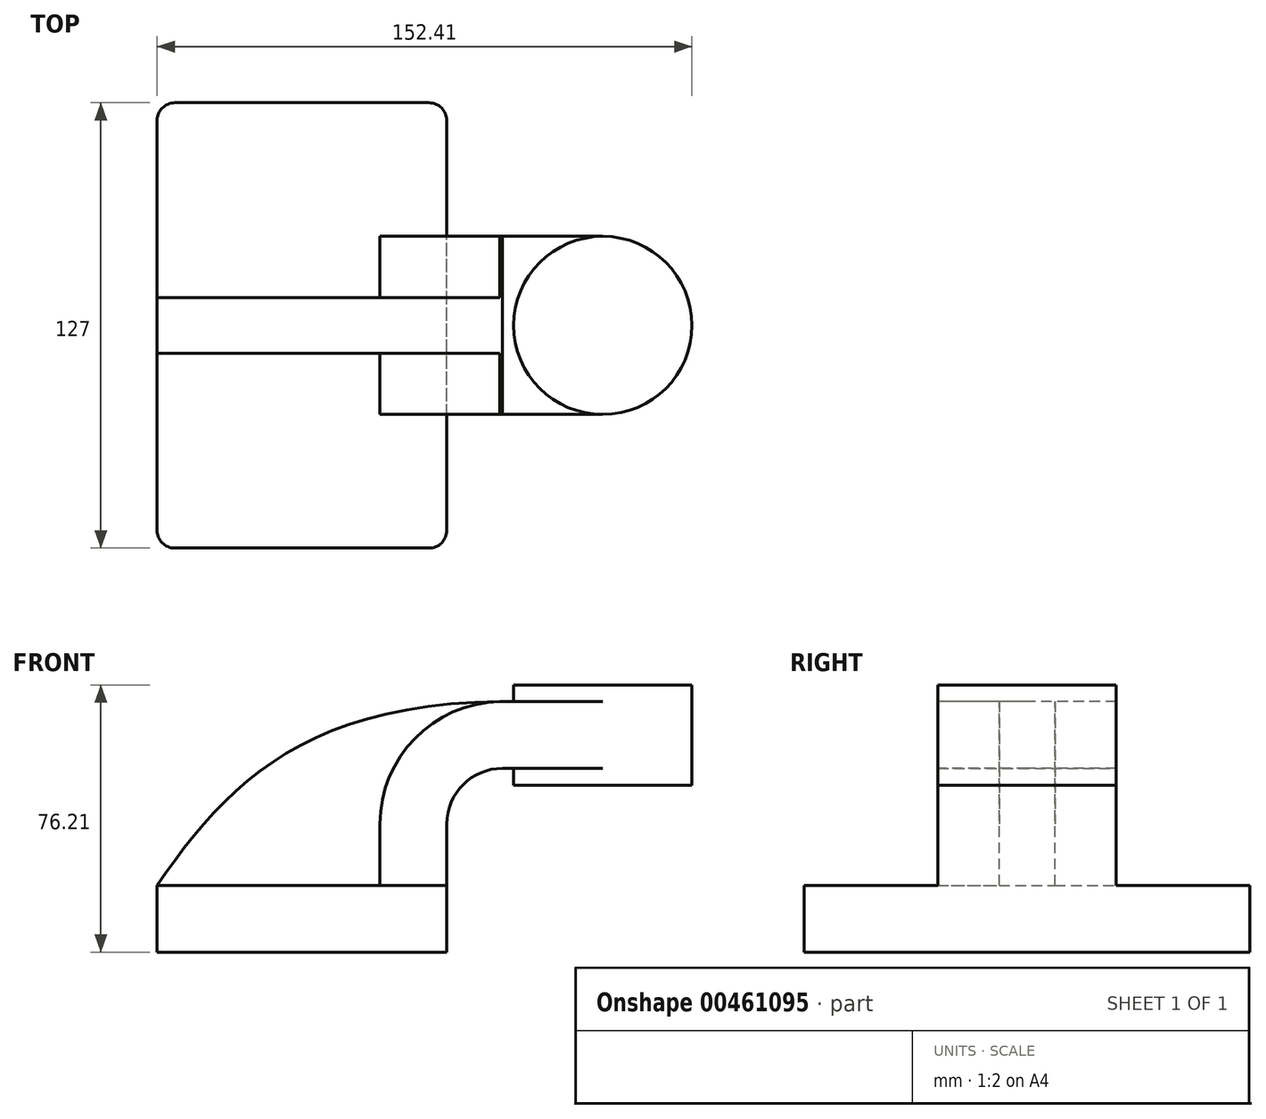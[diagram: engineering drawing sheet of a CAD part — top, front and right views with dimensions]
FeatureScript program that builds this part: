
annotation { "Feature Type Name" : "Feature", "Feature Type Description" : "" }
export const myFeature = defineFeature(function(context is Context, id is Id, definition is map)
    precondition{}
    {
        {
            var Q0;
            Q0=qCreatedBy(makeId("Front.planeOp"),FACE);
            var sketch = newSketch(context, id + "F0", { "sketchPlane" : qUnion([Q0])});
            skLineSegment(sketch, "E0.bottom", {"start": v(-41.28, 9.52) * mm, "end": v(41.28, 9.53) * mm});
            skLineSegment(sketch, "E0.top", {"start": v(-41.28, -9.53) * mm, "end": v(41.28, -9.53) * mm});
            skLineSegment(sketch, "E0.left", {"start": v(-41.28, 9.52) * mm, "end": v(-41.28, -9.53) * mm});
            skLineSegment(sketch, "E0.right", {"start": v(41.28, 9.53) * mm, "end": v(41.28, -9.52) * mm});
            skPoint(sketch, "E0.middle", {"position": v(0, 0) * mm});
            skLineSegment(sketch, "E1.bottom", {"start": v(111.12, 38.1) * mm, "end": v(60.33, 38.1) * mm});
            skLineSegment(sketch, "E1.top", {"start": v(111.12, 66.68) * mm, "end": v(60.33, 66.68) * mm});
            skLineSegment(sketch, "E1.left", {"start": v(111.12, 38.1) * mm, "end": v(111.12, 66.68) * mm});
            skLineSegment(sketch, "E1.right", {"start": v(60.33, 38.1) * mm, "end": v(60.33, 66.68) * mm});
            skPoint(sketch, "E1.middle", {"position": v(85.72, 52.39) * mm});
            skLineSegment(sketch, "E2", {"start": v(41.27, 9.53) * mm, "end": v(41.27, 27) * mm});
            skArc(sketch, "E3", {"start": v(41.27, 27) * mm, "mid": v(45.92, 38.23) * mm, "end": v(57.15, 42.88) * mm});
            skLineSegment(sketch, "E4", {"start": v(57.15, 42.88) * mm, "end": v(81.45, 42.88) * mm});
            skLineSegment(sketch, "E5.0", {"start": v(57.15, 61.93) * mm, "end": v(81.45, 61.93) * mm});
            skArc(sketch, "E5.1", {"start": v(22.22, 27) * mm, "mid": v(32.45, 51.7) * mm, "end": v(57.15, 61.93) * mm});
            skLineSegment(sketch, "E5.2", {"start": v(22.22, 9.53) * mm, "end": v(22.22, 27) * mm});
            skLineSegment(sketch, "E6", {"start": v(85.72, 38.1) * mm, "end": v(85.72, 66.68) * mm});
            skLineSegment(sketch, "E7", {"start": v(81.45, 61.93) * mm, "end": v(85.72, 61.93) * mm});
            skFitSpline(sketch, "E8", {"points": [v(-41.28, 9.52) * mm, v(57.15, 61.93) * mm], "startDerivative": vector(58.29, 84.47) * mm, "endDerivative": vector(171.45, 1.52) * mm});
            skLineSegment(sketch, "E9", {"start": v(81.45, 42.88) * mm, "end": v(85.72, 42.88) * mm});
            skSolve(sketch);
        }
        {
            var Q0;
            Q0=makeQuery(id+"F0.imprint","IMPRINT",FACE,{"disambiguationData":[TD([[makeQuery(id+"F0.imprint","IMPRINT",EDGE,{"derivedFrom":sQuery(id+"F0.wireOp",EDGE,"E0.top")}),1.0]])]});
            extrude(context, id + "F1", {"entities" : qUnion([Q0]), "endBound" : BoundingType.SYMMETRIC, "depth" : 127 * mm});
        }
        {
            var Q0;
            {var subQ6=sQuery(id+"F0.wireOp",EDGE,"E2");Q0=makeQuery(id+"F0.imprint","IMPRINT",FACE,{"disambiguationData":[TD([[makeQuery(id+"F0.imprint","IMPRINT",EDGE,{"derivedFrom":subQ6}),1.0]])]});}
            extrude(context, id + "F2", {"entities" : qUnion([Q0]), "operationType" : NewBodyOperationType.ADD, "endBound" : BoundingType.SYMMETRIC, "depth" : 50.8 * mm});
        }
        {
            var Q0;
            {var subQ3=sQuery(id+"F0.wireOp",EDGE,"E5.2");Q0=makeQuery(id+"F0.imprint","IMPRINT",FACE,{"disambiguationData":[TD([[makeQuery(id+"F0.imprint","IMPRINT",EDGE,{"derivedFrom":subQ3}),1.0]])]});}
            extrude(context, id + "F3", {"entities" : qUnion([Q0]), "operationType" : NewBodyOperationType.ADD, "endBound" : BoundingType.SYMMETRIC, "depth" : 15.88 * mm});
        }
        {
            var Q0;
            {var subQ0=sQuery(id+"F0.wireOp",EDGE,"E7");Q0=makeQuery(id+"F0.imprint","IMPRINT",FACE,{"disambiguationData":[TD([[makeQuery(id+"F0.imprint","IMPRINT",EDGE,{"derivedFrom":subQ0}),-1.0]])]});}
            extrude(context, id + "F4", {"entities" : qUnion([Q0]), "operationType" : NewBodyOperationType.ADD, "endBound" : BoundingType.SYMMETRIC, "depth" : 50.8 * mm});
        }
        {
            var Q0;
            {var subQ4=sQuery(id+"F0.wireOp",EDGE,"E1.left");Q0=makeQuery(id+"F0.imprint","IMPRINT",FACE,{"disambiguationData":[TD([[makeQuery(id+"F0.imprint","IMPRINT",EDGE,{"derivedFrom":subQ4}),1.0]])]});}
            var Q1;
            Q1=sQuery(id+"F0.wireOp",EDGE,"E6");
            revolve(context, id + "F5", {"operationType" : NewBodyOperationType.ADD, "entities" : qUnion([Q0]), "axis" : qUnion([Q1]), "revolveType" : RevolveType.FULL});
        }
        {
            var Q0;
            Q0=makeQuery(id+"F1.opExtrude","CAP_EDGE",EDGE,{"disambiguationData":[OSD([sQuery(id+"F0.wireOp",EDGE,"E0.left")])],"isStart":false});
            var Q1;
            Q1=makeQuery(id+"F1.opExtrude","CAP_EDGE",EDGE,{"disambiguationData":[OSD([sQuery(id+"F0.wireOp",EDGE,"E0.right")])],"isStart":false});
            var Q2;
            Q2=makeQuery(id+"F1.opExtrude","CAP_EDGE",EDGE,{"disambiguationData":[OSD([sQuery(id+"F0.wireOp",EDGE,"E0.right")])],"isStart":true});
            fillet(context, id + "F6", {"entities" : qUnion([Q0, Q1, Q2]), "radius" : 5.08 * mm, "tangentPropagation" : true, "allowEdgeOverflow" : false});
        }
        {
            var Q0;
            Q0=makeQuery(id+"F1.opExtrude","CAP_EDGE",EDGE,{"disambiguationData":[OSD([sQuery(id+"F0.wireOp",EDGE,"E0.left")])],"isStart":true});
            fillet(context, id + "F7", {"entities" : qUnion([Q0]), "radius" : 5.08 * mm, "tangentPropagation" : true, "allowEdgeOverflow" : false});
        }
    });
